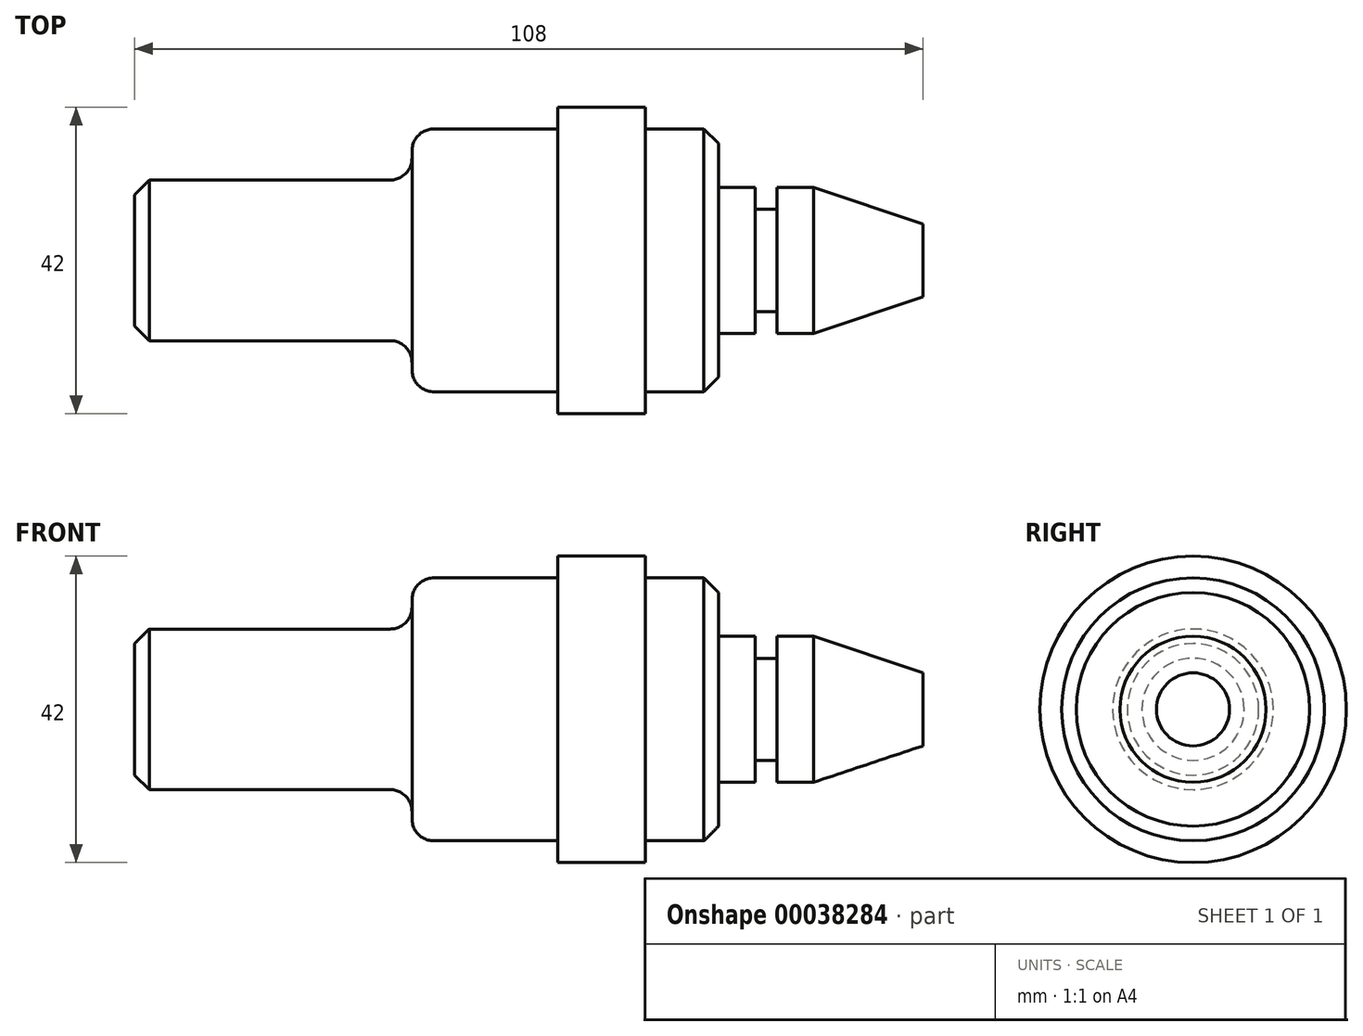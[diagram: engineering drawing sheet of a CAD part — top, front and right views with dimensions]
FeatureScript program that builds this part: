
annotation { "Feature Type Name" : "Feature", "Feature Type Description" : "" }
export const myFeature = defineFeature(function(context is Context, id is Id, definition is map)
    precondition{}
    {
        {
            var Q0;
            Q0=qCreatedBy(makeId("Front.planeOp"),FACE);
            var sketch = newSketch(context, id + "F0", { "sketchPlane" : qUnion([Q0])});
            skLineSegment(sketch, "E0", {"start": v(-84.05, 10) * mm, "end": v(23.95, 10) * mm});
            skLineSegment(sketch, "E1", {"start": v(23.95, 10) * mm, "end": v(23.95, 5) * mm});
            skLineSegment(sketch, "E2", {"start": v(23.95, 5) * mm, "end": v(8.95, 0) * mm});
            skLineSegment(sketch, "E3", {"start": v(8.95, 0) * mm, "end": v(3.95, 0) * mm});
            skLineSegment(sketch, "E4", {"start": v(3.95, 0) * mm, "end": v(3.95, 3) * mm});
            skLineSegment(sketch, "E5", {"start": v(3.95, 3) * mm, "end": v(0.95, 3) * mm});
            skLineSegment(sketch, "E6", {"start": v(0.95, 3) * mm, "end": v(0.95, 0) * mm});
            skLineSegment(sketch, "E7", {"start": v(0.95, 0) * mm, "end": v(-4.05, 0) * mm});
            skLineSegment(sketch, "E8", {"start": v(-4.05, 0) * mm, "end": v(-4.05, -8) * mm});
            skLineSegment(sketch, "E9", {"start": v(-4.05, -8) * mm, "end": v(-14.05, -8) * mm});
            skLineSegment(sketch, "E10", {"start": v(-14.05, -8) * mm, "end": v(-14.05, -11) * mm});
            skLineSegment(sketch, "E11", {"start": v(-14.05, -11) * mm, "end": v(-26.05, -11) * mm});
            skLineSegment(sketch, "E12", {"start": v(-26.05, -11) * mm, "end": v(-26.05, -8) * mm});
            skLineSegment(sketch, "E13", {"start": v(-26.05, -8) * mm, "end": v(-46.05, -8) * mm});
            skLineSegment(sketch, "E14", {"start": v(-46.05, -8) * mm, "end": v(-46.05, -1) * mm});
            skLineSegment(sketch, "E15", {"start": v(-46.05, -1) * mm, "end": v(-84.05, -1) * mm});
            skLineSegment(sketch, "E16", {"start": v(-84.05, -1) * mm, "end": v(-84.05, 10) * mm});
            skLineSegment(sketch, "E17", {"start": v(-84.05, 10) * mm, "end": v(-128.4, 10) * mm, "construction": true});
            skSolve(sketch);
        }
        {
            var Q0;
            Q0 = qSketchRegion(id + "F0", true);
            var Q1;
            Q1=sQuery(id+"F0.wireOp",EDGE,"E17");
            revolve(context, id + "F1", {"entities" : qUnion([Q0]), "axis" : qUnion([Q1]), "revolveType" : RevolveType.FULL});
        }
        {
            var Q0;
            Q0=makeQuery(id+"F1.opRevolve","SWEPT_EDGE",EDGE,{"disambiguationData":[OSD([sQuery(id+"F0.wireOp",EDGE,"E15"),sQuery(id+"F0.wireOp",EDGE,"E16")])]});
            var Q1;
            Q1=makeQuery(id+"F1.opRevolve","SWEPT_EDGE",EDGE,{"disambiguationData":[OSD([sQuery(id+"F0.wireOp",EDGE,"E8"),sQuery(id+"F0.wireOp",EDGE,"E9")])]});
            chamfer(context, id + "F2", {"entities" : qUnion([Q0, Q1]), "width" : 2 * mm, "tangentPropagation" : true});
        }
        {
            var Q0;
            Q0=makeQuery(id+"F1.opRevolve","SWEPT_EDGE",EDGE,{"disambiguationData":[OSD([sQuery(id+"F0.wireOp",EDGE,"E13"),sQuery(id+"F0.wireOp",EDGE,"E14")])]});
            fillet(context, id + "F3", {"entities" : qUnion([Q0]), "radius" : 3 * mm, "tangentPropagation" : true, "allowEdgeOverflow" : false});
        }
        {
            var Q0;
            Q0=makeQuery(id+"F1.opRevolve","SWEPT_EDGE",EDGE,{"disambiguationData":[OSD([sQuery(id+"F0.wireOp",EDGE,"E14"),sQuery(id+"F0.wireOp",EDGE,"E15")])]});
            fillet(context, id + "F4", {"entities" : qUnion([Q0]), "radius" : 3 * mm, "tangentPropagation" : true, "allowEdgeOverflow" : false});
        }
    });
